# Revit family: Magnuson-Parban-Space_Divider--
name_source: partatom
category: Furniture
revit_build: Autodesk Revit 2016 (Build: 20150220_1215(x64)
units: mm (PartAtom-declared; Revit-internal decimal feet)

## family parameters
Always vertical = Yes
Cut with Voids When Loaded = No
OmniClass Number = 23.40.20.00
OmniClass Title = General Furniture and Specialties
Room Calculation Point = No
Shared = No
Work Plane-Based = No

## types (2) — shared parameters
Assembly Code = E2020200
Base Finish = MAG - Natural Oak
Depth = 18"
Frame Finish = MAG - Paint Matte White
Glide Finish = MAG - Plastic Black
Keynote = 12500
Low Emitting Finish = Yes
Low Emitting Material = Yes
Manufacturer = Magnuson Group
Salvage or Reuse = Yes
Screen Finish = MAG - Aluminum Mesh
Type Comments = Parban
URL = www.magnusongroup.com
Width = 37 3/8"
zero-valued in all types: Percentage of Recycled Content

## per-type parameters (varying)
| type | Description | Height |
| PARBAN-L | Space Dividers 71 1/2"H | 71 1/2" |
| PARBAN-S | Space Dividers 51 1/4"H | 51 1/4" |

note: column(s) folded — value = type name in every type: Model

## geometry (parser evidence)
native form markers: Sweep x1
no freeform markers — native parametric forms only
